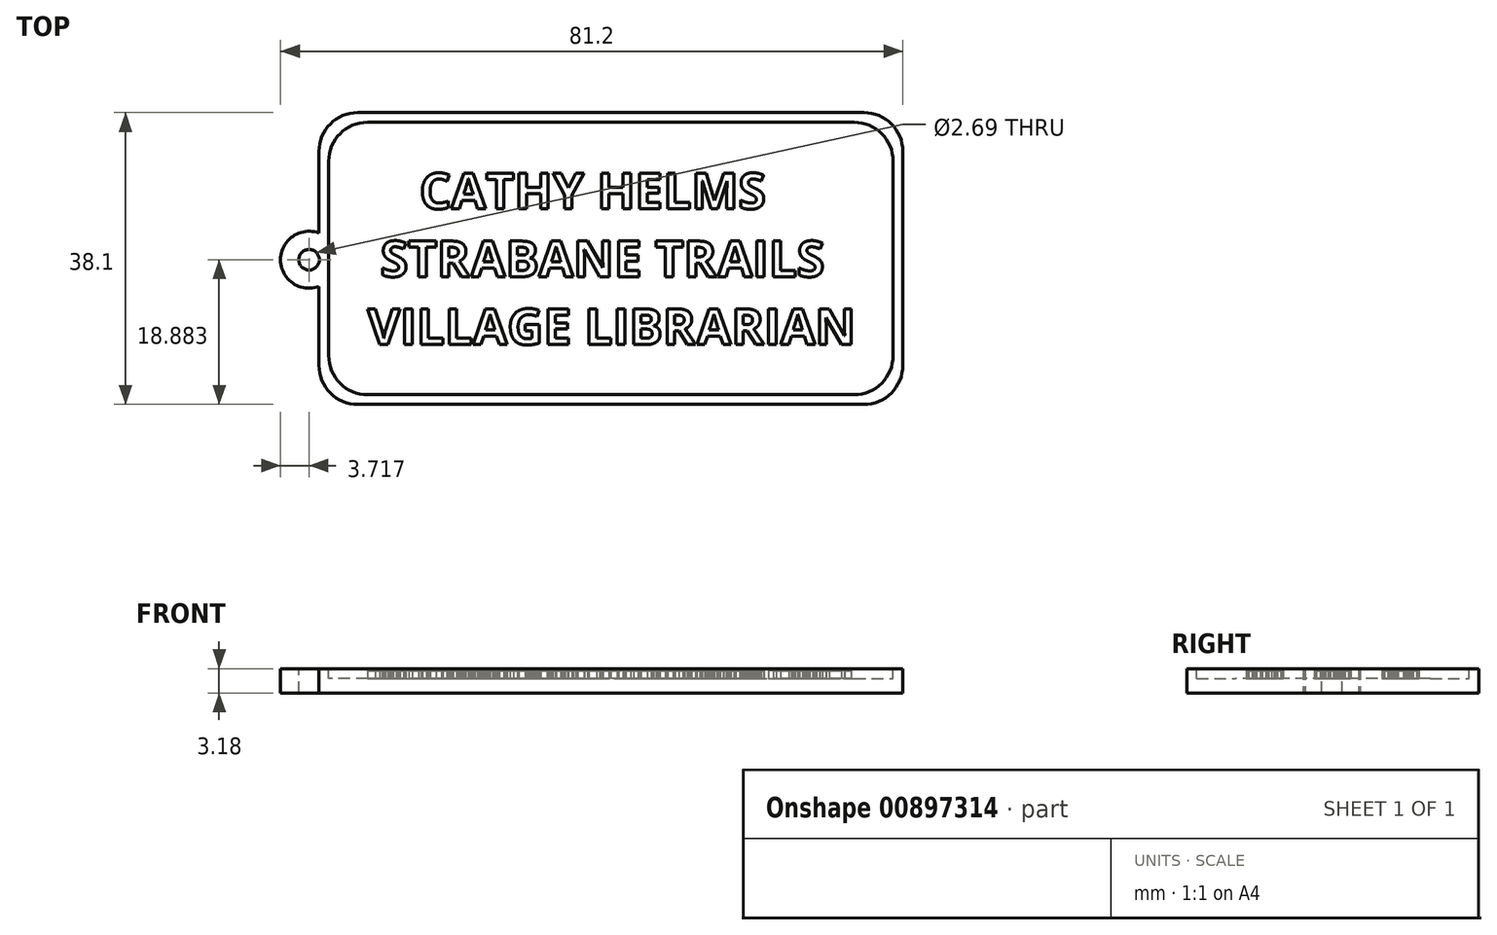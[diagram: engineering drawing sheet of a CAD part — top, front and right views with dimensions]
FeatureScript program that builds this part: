
annotation { "Feature Type Name" : "Feature", "Feature Type Description" : "" }
export const myFeature = defineFeature(function(context is Context, id is Id, definition is map)
    precondition{}
    {
        {
            var Q0;
            Q0=qCreatedBy(makeId("Top.planeOp"),FACE);
            var sketch = newSketch(context, id + "F0", { "sketchPlane" : qUnion([Q0])});
            skLineSegment(sketch, "E0.right", {"start": v(59.03, 19.05) * mm, "end": v(59.03, -19.05) * mm});
            skArc(sketch, "E1", {"start": v(-17.17, 3.32) * mm, "mid": v(-22.17, -0.17) * mm, "end": v(-17.17, -3.66) * mm});
            skPoint(sketch, "E1.centerSnap0", {"position": v(-22.6, -0.17) * mm});
            skLineSegment(sketch, "E2", {"start": v(-17.17, 3.32) * mm, "end": v(-17.17, 19.05) * mm});
            skLineSegment(sketch, "E3", {"start": v(-17.17, -3.66) * mm, "end": v(-17.17, -19.05) * mm});
            skPoint(sketch, "E4.orphan", {"position": v(-22.6, 14.34) * mm});
            skPoint(sketch, "E5.orphan", {"position": v(-22.6, -14.68) * mm});
            skLineSegment(sketch, "E6", {"start": v(-17.17, 19.05) * mm, "end": v(59.03, 19.05) * mm});
            skLineSegment(sketch, "E7", {"start": v(-17.17, -19.05) * mm, "end": v(59.03, -19.05) * mm});
            skSolve(sketch);
        }
        {
            var Q0;
            Q0=makeQuery(id+"F0.imprint","IMPRINT",FACE,{"disambiguationData":[TD([[makeQuery(id+"F0.imprint","IMPRINT",EDGE,{"derivedFrom":sQuery(id+"F0.wireOp",EDGE,"E0.right")}),-1.0]])]});
            extrude(context, id + "F1", {"entities" : qUnion([Q0]), "endBound" : BoundingType.SYMMETRIC, "depth" : 3.17 * mm, "offsetDistance" : 25.4 * mm});
        }
        {
            var Q0;
            {var subQ0=sQuery(id+"F0.wireOp",EDGE,"E1");var subQ1=sQuery(id+"F0.wireOp",EDGE,"E3");var subQ2=sQuery(id+"F0.wireOp",EDGE,"E0.right");var subQ3=sQuery(id+"F0.wireOp",EDGE,"E6");var subQ4=sQuery(id+"F0.wireOp",EDGE,"E7");var subQ5=sQuery(id+"F0.wireOp",EDGE,"E2");Q0=makeQuery(id+"FPCTxZ15ulyRdRa_1.boolean.opBoolean","SPLIT",FACE,{"disambiguationData":[TD([makeQuery(id+"F1.opExtrude","SWEPT_FACE",FACE,{"disambiguationData":[OSD([subQ2])]})])],"derivedFrom":makeQuery(id+"F1.opExtrude","CAP_FACE",FACE,{"disambiguationData":[OSD([subQ2,subQ0,subQ5,subQ1,subQ3,subQ4])],"isStart":false})});}
            var sketch = newSketch(context, id + "F2", { "sketchPlane" : qUnion([Q0])});
            skCircle(sketch, "E8", {"center": v(-18.45, -0.17) * mm, "radius": 1.35 * mm});
            skSolve(sketch);
        }
        {
            var Q0;
            Q0=makeQuery(id+"F2.imprint","IMPRINT",FACE,{"disambiguationData":[TD([[makeQuery(id+"F2.imprint","IMPRINT",EDGE,{"derivedFrom":sQuery(id+"F2.wireOp",EDGE,"E8")}),1.0]])]});
            extrude(context, id + "F3", {"entities" : qUnion([Q0]), "operationType" : NewBodyOperationType.REMOVE, "endBound" : BoundingType.THROUGH_ALL, "oppositeDirection" : true, "depth" : 25.4 * mm, "offsetDistance" : 25.4 * mm});
        }
        {
            var Q0;
            Q0=makeQuery(id+"F1.opExtrude","CAP_FACE",FACE,{"disambiguationData":[OSD([sQuery(id+"F0.wireOp",EDGE,"E0.right"),sQuery(id+"F0.wireOp",EDGE,"E1"),sQuery(id+"F0.wireOp",EDGE,"E2"),sQuery(id+"F0.wireOp",EDGE,"E3"),sQuery(id+"F0.wireOp",EDGE,"E6"),sQuery(id+"F0.wireOp",EDGE,"E7")])],"isStart":false});
            var sketch = newSketch(context, id + "F4", { "sketchPlane" : qUnion([Q0])});
            skLineSegment(sketch, "E9.bottom", {"start": v(-15.9, 17.78) * mm, "end": v(57.76, 17.78) * mm});
            skLineSegment(sketch, "E9.top", {"start": v(-15.9, -17.78) * mm, "end": v(57.76, -17.78) * mm});
            skLineSegment(sketch, "E9.left", {"start": v(-15.9, 17.78) * mm, "end": v(-15.9, -17.78) * mm});
            skLineSegment(sketch, "E9.right", {"start": v(57.76, 17.78) * mm, "end": v(57.76, -17.78) * mm});
            skSolve(sketch);
        }
        {
            var Q0;
            Q0=makeQuery(id+"F4.imprint","IMPRINT",FACE,{"disambiguationData":[TD([[makeQuery(id+"F4.imprint","IMPRINT",EDGE,{"derivedFrom":sQuery(id+"F4.wireOp",EDGE,"E9.bottom")}),-1.0]])]});
            extrude(context, id + "F5", {"entities" : qUnion([Q0]), "operationType" : NewBodyOperationType.REMOVE, "oppositeDirection" : true, "depth" : 1.27 * mm, "offsetDistance" : 25.4 * mm});
        }
        {
            var Q0;
            Q0=makeQuery(id+"F5.boolean.opBoolean","COPY",FACE,{"derivedFrom":makeQuery(id+"F5.opExtrude","CAP_FACE",FACE,{"disambiguationData":[OSD([sQuery(id+"F4.wireOp",EDGE,"E9.bottom"),sQuery(id+"F4.wireOp",EDGE,"E9.top"),sQuery(id+"F4.wireOp",EDGE,"E9.left"),sQuery(id+"F4.wireOp",EDGE,"E9.right")])],"isStart":false})});
            var sketch = newSketch(context, id + "F6", { "sketchPlane" : qUnion([Q0])});
            skText(sketch, "E10", { "text": "    CATHY HELMS\n STRABANE TRAILS \nVILLAGE LIBRARIAN\n", "fontName": "OpenSans-Bold.ttf"});
            skLineSegment(sketch, "E11", {"start": v(20.93, 20.85) * mm, "end": v(20.93, 16.13) * mm});
            const initialGuessF6  = {"E10": [-0.01082, 0.00648, 1, 0, 0.00469]};
            skSetInitialGuess(sketch, initialGuessF6);
            skSolve(sketch);
        }
        {
            var Q0;
            Q0 = qSketchRegion(id + "F6", true);
            extrude(context, id + "F7", {"entities" : qUnion([Q0]), "operationType" : NewBodyOperationType.ADD, "depth" : 1.02 * mm, "offsetDistance" : 25.4 * mm});
        }
        {
            var Q0;
            Q0=makeQuery(id+"F1.opExtrude","SWEPT_EDGE",EDGE,{"disambiguationData":[OSD([sQuery(id+"F0.wireOp",EDGE,"E2"),sQuery(id+"F0.wireOp",EDGE,"E6")])]});
            var Q1;
            Q1=makeQuery(id+"F1.opExtrude","SWEPT_EDGE",EDGE,{"disambiguationData":[OSD([sQuery(id+"F0.wireOp",EDGE,"E0.right"),sQuery(id+"F0.wireOp",EDGE,"E6")])]});
            var Q2;
            Q2=makeQuery(id+"F1.opExtrude","SWEPT_EDGE",EDGE,{"disambiguationData":[OSD([sQuery(id+"F0.wireOp",EDGE,"E0.right"),sQuery(id+"F0.wireOp",EDGE,"E7")])]});
            var Q3;
            Q3=makeQuery(id+"F1.opExtrude","SWEPT_EDGE",EDGE,{"disambiguationData":[OSD([sQuery(id+"F0.wireOp",EDGE,"E3"),sQuery(id+"F0.wireOp",EDGE,"E7")])]});
            var Q4;
            Q4=makeQuery(id+"F5.boolean.opBoolean","COPY",EDGE,{"derivedFrom":makeQuery(id+"F5.opExtrude","SWEPT_EDGE",EDGE,{"disambiguationData":[OSD([sQuery(id+"F4.wireOp",EDGE,"E9.bottom"),sQuery(id+"F4.wireOp",EDGE,"E9.left")])]})});
            var Q5;
            Q5=makeQuery(id+"F5.boolean.opBoolean","COPY",EDGE,{"derivedFrom":makeQuery(id+"F5.opExtrude","SWEPT_EDGE",EDGE,{"disambiguationData":[OSD([sQuery(id+"F4.wireOp",EDGE,"E9.top"),sQuery(id+"F4.wireOp",EDGE,"E9.left")])]})});
            var Q6;
            Q6=makeQuery(id+"F5.boolean.opBoolean","COPY",EDGE,{"derivedFrom":makeQuery(id+"F5.opExtrude","SWEPT_EDGE",EDGE,{"disambiguationData":[OSD([sQuery(id+"F4.wireOp",EDGE,"E9.bottom"),sQuery(id+"F4.wireOp",EDGE,"E9.right")])]})});
            var Q7;
            Q7=makeQuery(id+"F5.boolean.opBoolean","COPY",EDGE,{"derivedFrom":makeQuery(id+"F5.opExtrude","SWEPT_EDGE",EDGE,{"disambiguationData":[OSD([sQuery(id+"F4.wireOp",EDGE,"E9.top"),sQuery(id+"F4.wireOp",EDGE,"E9.right")])]})});
            fillet(context, id + "F8", {"entities" : qUnion([Q0, Q1, Q2, Q3, Q4, Q5, Q6, Q7]), "tangentPropagation" : true, "radius" : 5.08 * mm, "defaultsChanged" : true, "vertexSettings" : [], "allowEdgeOverflow" : false});
        }
    });
